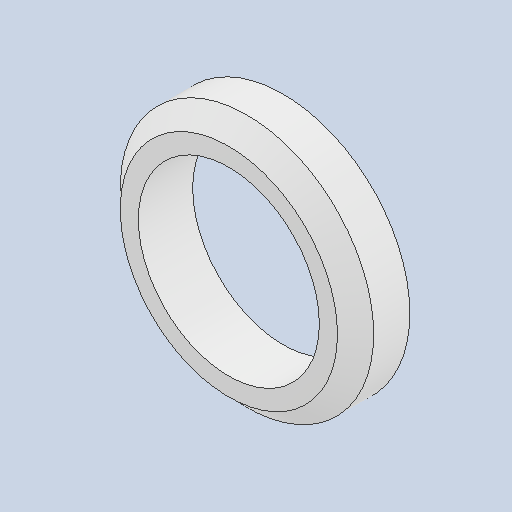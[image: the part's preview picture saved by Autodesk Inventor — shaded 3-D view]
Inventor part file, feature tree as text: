
AUTODESK INVENTOR PART (.ipt)
format: ipt  version: 2023 (Build 270158030, 158C)  size: 105,984 bytes
history: native  units: mm
features: other x3, sketch x1
ambient origin geometry x8: Origin, YZ Plane, XZ Plane, XY Plane, X Axis, Y Axis, Z Axis, Center Point
bodies: Solid1 (feature_tree)
feature tree (4):
  other  "w1.5f5-7n.ipt"
  other  "Solid1::w1.5f5-7n.ipt"
  other  "TaggingFeature1"
  sketch  "Sketch1"  dims[d0=10.0mm]
